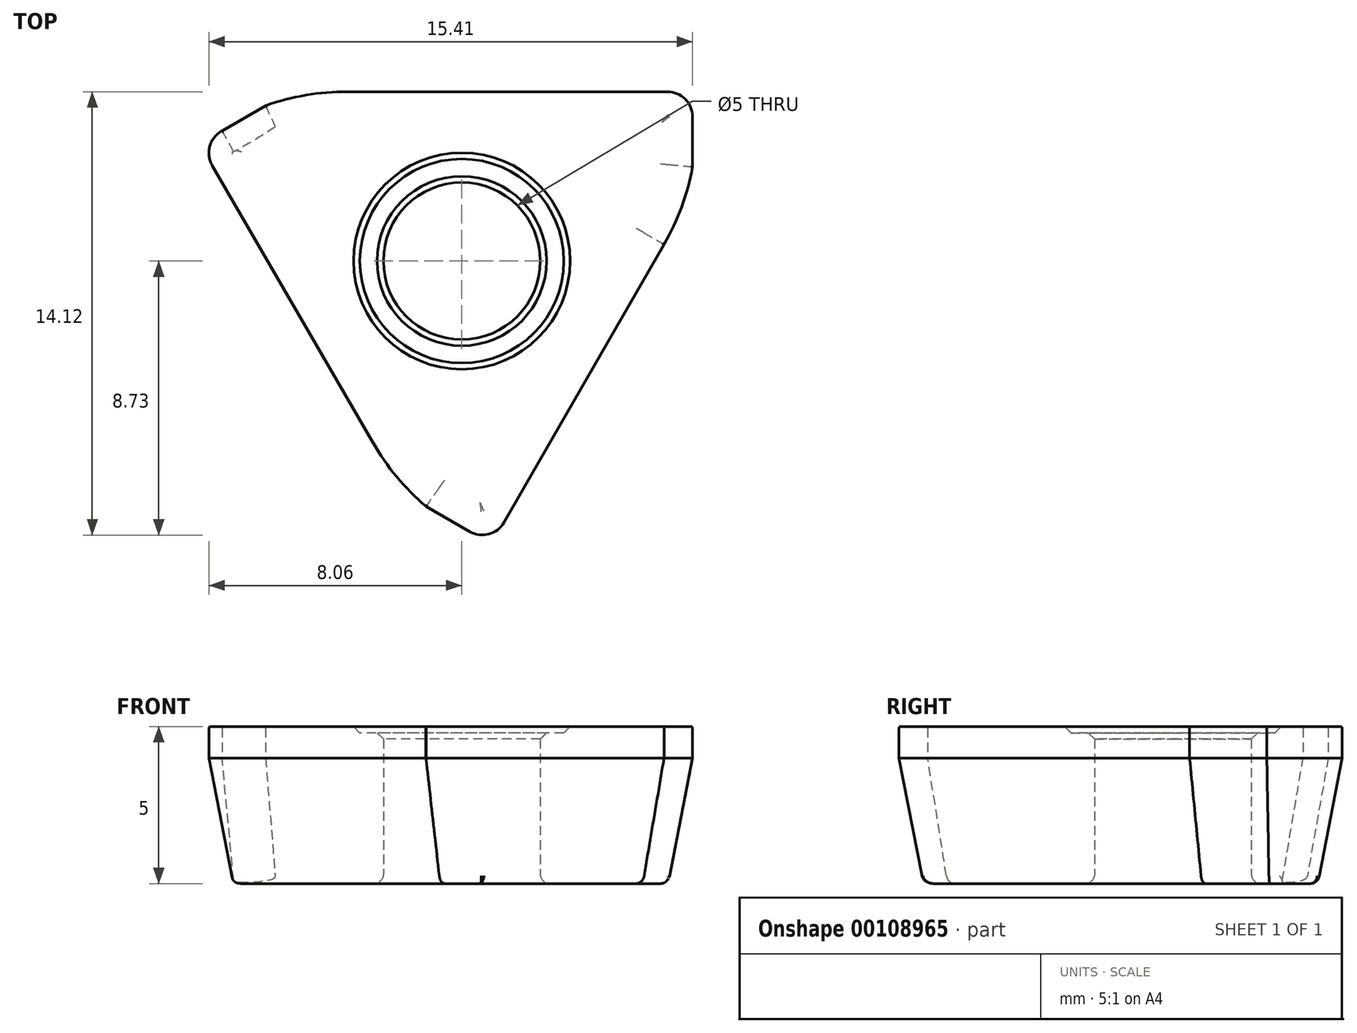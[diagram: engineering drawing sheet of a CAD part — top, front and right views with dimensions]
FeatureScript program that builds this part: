
annotation { "Feature Type Name" : "Feature", "Feature Type Description" : "" }
export const myFeature = defineFeature(function(context is Context, id is Id, definition is map)
    precondition{}
    {
        {
            var Q0;
            Q0=qCreatedBy(makeId("Top.planeOp"),FACE);
            var sketch = newSketch(context, id + "F0", { "sketchPlane" : qUnion([Q0])});
            skLineSegment(sketch, "E0", {"start": v(-2.83, -5.78) * mm, "end": v(-7.95, 3.04) * mm});
            skLineSegment(sketch, "E1", {"start": v(7.35, 4.6) * mm, "end": v(7.35, 3) * mm});
            skLineSegment(sketch, "E2", {"start": v(0.25, -8.62) * mm, "end": v(-1.13, -7.82) * mm});
            skPoint(sketch, "E3.orphan", {"position": v(0, -10.66) * mm});
            skPoint(sketch, "E4.visualSharp", {"position": v(-8.35, 3.74) * mm});
            skArc(sketch, "E4.filletArc", {"start": v(-7.64, 4.15) * mm, "mid": v(-8.03, 3.66) * mm, "end": v(-7.95, 3.04) * mm});
            skPoint(sketch, "E5.visualSharp", {"position": v(0.95, -9.02) * mm});
            skArc(sketch, "E5.filletArc", {"start": v(0.25, -8.62) * mm, "mid": v(0.86, -8.7) * mm, "end": v(1.34, -8.33) * mm});
            skPoint(sketch, "E6.visualSharp", {"position": v(7.35, 5.4) * mm});
            skArc(sketch, "E6.filletArc", {"start": v(7.35, 4.6) * mm, "mid": v(7.12, 5.16) * mm, "end": v(6.55, 5.4) * mm});
            skPoint(sketch, "E7", {"position": v(-6.25, 4.95) * mm});
            skPoint(sketch, "E8", {"position": v(-3.65, 5.4) * mm});
            skPoint(sketch, "E9", {"position": v(7.35, 3) * mm});
            skPoint(sketch, "E10", {"position": v(-1.13, -7.82) * mm});
            skPoint(sketch, "E11", {"position": v(-2.83, -5.78) * mm});
            skPoint(sketch, "E12", {"position": v(6.43, 0.51) * mm});
            skCircle(sketch, "E13", {"center": v(0, 0) * mm, "radius": 2.5 * mm});
            skArc(sketch, "E14", {"start": v(-3.65, 5.4) * mm, "mid": v(-4.97, 5.28) * mm, "end": v(-6.25, 4.95) * mm});
            skLineSegment(sketch, "E15", {"start": v(-7.64, 4.15) * mm, "end": v(-6.25, 4.95) * mm});
            skLineSegment(sketch, "E16", {"start": v(-3.65, 5.4) * mm, "end": v(6.55, 5.4) * mm});
            skArc(sketch, "E17.1.0", {"start": v(-2.83, -5.78) * mm, "mid": v(-2.08, -6.87) * mm, "end": v(-1.15, -7.81) * mm});
            skArc(sketch, "E17.2.0", {"start": v(6.44, 0.53) * mm, "mid": v(7, 1.72) * mm, "end": v(7.35, 3) * mm});
            skPoint(sketch, "E17.center", {"position": v(-0.02, 0.04) * mm});
            skPoint(sketch, "E18.orphan", {"position": v(7.35, 2.1) * mm});
            skCircle(sketch, "E19", {"center": v(0, 0) * mm, "radius": 3.25 * mm});
            skLineSegment(sketch, "E20.trimOffspring", {"start": v(6.43, 0.51) * mm, "end": v(1.34, -8.33) * mm});
            skLineSegment(sketch, "E21", {"start": v(6.43, 0.51) * mm, "end": v(6.44, 0.53) * mm});
            skLineSegment(sketch, "E22", {"start": v(-1.15, -7.81) * mm, "end": v(-1.13, -7.82) * mm});
            skSolve(sketch);
        }
        {
            var Q0;
            Q0=makeQuery(id+"F0.imprint","IMPRINT",FACE,{"disambiguationData":[TD([[makeQuery(id+"F0.imprint","IMPRINT",EDGE,{"derivedFrom":sQuery(id+"F0.wireOp",EDGE,"E0")}),-1.0]])]});
            extrude(context, id + "F1", {"entities" : qUnion([Q0]), "depth" : 5 * mm});
        }
        {
            var Q0;
            Q0=makeQuery(id+"F0.imprint","IMPRINT",FACE,{"disambiguationData":[TD([[makeQuery(id+"F0.imprint","IMPRINT",EDGE,{"derivedFrom":sQuery(id+"F0.wireOp",EDGE,"E13")}),-1.0]])]});
            var Q1;
            Q1=makeQuery(id+"F0.imprint","IMPRINT",FACE,{"disambiguationData":[TD([[makeQuery(id+"F0.imprint","IMPRINT",EDGE,{"derivedFrom":sQuery(id+"F0.wireOp",EDGE,"E0")}),-1.0]])]});
            extrude(context, id + "F2", {"entities" : qUnion([Q0, Q1]), "operationType" : NewBodyOperationType.ADD, "depth" : 4.8 * mm});
        }
        {
            var Q0;
            Q0=makeQuery(id+"F1.opExtrude","CAP_EDGE",EDGE,{"disambiguationData":[OSD([sQuery(id+"F0.wireOp",EDGE,"E0")])],"isStart":true});
            var Q1;
            Q1=makeQuery(id+"F1.opExtrude","CAP_EDGE",EDGE,{"disambiguationData":[OSD([sQuery(id+"F0.wireOp",EDGE,"E17.1.0")])],"isStart":true});
            var Q2;
            Q2=makeQuery(id+"F1.opExtrude","CAP_EDGE",EDGE,{"disambiguationData":[OSD([sQuery(id+"F0.wireOp",EDGE,"E16")])],"isStart":true});
            var Q3;
            Q3=makeQuery(id+"F1.opExtrude","CAP_EDGE",EDGE,{"disambiguationData":[OSD([sQuery(id+"F0.wireOp",EDGE,"E15")])],"isStart":true});
            var Q4;
            Q4=makeQuery(id+"F1.opExtrude","CAP_EDGE",EDGE,{"disambiguationData":[OSD([sQuery(id+"F0.wireOp",EDGE,"E4.filletArc")])],"isStart":true});
            var Q5;
            Q5=makeQuery(id+"F1.opExtrude","CAP_EDGE",EDGE,{"disambiguationData":[OSD([sQuery(id+"F0.wireOp",EDGE,"E14")])],"isStart":true});
            var Q6;
            Q6=makeQuery(id+"F1.opExtrude","CAP_EDGE",EDGE,{"disambiguationData":[OSD([sQuery(id+"F0.wireOp",EDGE,"E1")])],"isStart":true});
            var Q7;
            Q7=makeQuery(id+"F1.opExtrude","CAP_EDGE",EDGE,{"disambiguationData":[OSD([sQuery(id+"F0.wireOp",EDGE,"E20.trimOffspring")])],"isStart":true});
            var Q8;
            Q8=makeQuery(id+"F1.opExtrude","CAP_EDGE",EDGE,{"disambiguationData":[OSD([sQuery(id+"F0.wireOp",EDGE,"E6.filletArc")])],"isStart":true});
            var Q9;
            Q9=makeQuery(id+"F1.opExtrude","CAP_EDGE",EDGE,{"disambiguationData":[OSD([sQuery(id+"F0.wireOp",EDGE,"E2")])],"isStart":true});
            var Q10;
            Q10=makeQuery(id+"F1.opExtrude","CAP_EDGE",EDGE,{"disambiguationData":[OSD([sQuery(id+"F0.wireOp",EDGE,"E21")])],"isStart":true});
            var Q11;
            Q11=makeQuery(id+"F1.opExtrude","CAP_EDGE",EDGE,{"disambiguationData":[OSD([sQuery(id+"F0.wireOp",EDGE,"E17.2.0")])],"isStart":true});
            var Q12;
            Q12=makeQuery(id+"F1.opExtrude","CAP_EDGE",EDGE,{"disambiguationData":[OSD([sQuery(id+"F0.wireOp",EDGE,"E5.filletArc")])],"isStart":true});
            chamfer(context, id + "F3", {"entities" : qUnion([Q0, Q1, Q2, Q3, Q4, Q5, Q6, Q7, Q8, Q9, Q10, Q11, Q12]), "chamferType" : ChamferType.OFFSET_ANGLE, "width" : 4 * mm, "oppositeDirection" : true, "angle" : 11 * degree});
        }
        {
            var Q0;
            Q0=makeQuery(id+"F1.opExtrude","CAP_EDGE",EDGE,{"disambiguationData":[OSD([sQuery(id+"F0.wireOp",EDGE,"E0")])],"isStart":false});
            var Q1;
            Q1=makeQuery(id+"F1.opExtrude","CAP_EDGE",EDGE,{"disambiguationData":[OSD([sQuery(id+"F0.wireOp",EDGE,"E4.filletArc")])],"isStart":false});
            var Q2;
            Q2=makeQuery(id+"F1.opExtrude","CAP_EDGE",EDGE,{"disambiguationData":[OSD([sQuery(id+"F0.wireOp",EDGE,"E15")])],"isStart":false});
            var Q3;
            Q3=makeQuery(id+"F1.opExtrude","CAP_EDGE",EDGE,{"disambiguationData":[OSD([sQuery(id+"F0.wireOp",EDGE,"E17.1.0")])],"isStart":false});
            var Q4;
            Q4=makeQuery(id+"F1.opExtrude","CAP_EDGE",EDGE,{"disambiguationData":[OSD([sQuery(id+"F0.wireOp",EDGE,"E2")])],"isStart":false});
            var Q5;
            Q5=makeQuery(id+"F1.opExtrude","CAP_EDGE",EDGE,{"disambiguationData":[OSD([sQuery(id+"F0.wireOp",EDGE,"E16")])],"isStart":false});
            var Q6;
            Q6=makeQuery(id+"F1.opExtrude","CAP_EDGE",EDGE,{"disambiguationData":[OSD([sQuery(id+"F0.wireOp",EDGE,"E14")])],"isStart":false});
            var Q7;
            Q7=makeQuery(id+"F1.opExtrude","CAP_EDGE",EDGE,{"disambiguationData":[OSD([sQuery(id+"F0.wireOp",EDGE,"E17.2.0")])],"isStart":false});
            fillet(context, id + "F4", {"entities" : qUnion([Q0, Q1, Q2, Q3, Q4, Q5, Q6, Q7]), "radius" : 0.05 * mm, "tangentPropagation" : true, "allowEdgeOverflow" : false});
        }
        {
            var Q0;
            {var subQ0=sQuery(id+"F0.wireOp",EDGE,"E22");var subQ1=sQuery(id+"F0.wireOp",EDGE,"E21");var subQ2=sQuery(id+"F0.wireOp",EDGE,"E20.trimOffspring");var subQ3=sQuery(id+"F0.wireOp",EDGE,"E17.2.0");var subQ4=sQuery(id+"F0.wireOp",EDGE,"E17.1.0");var subQ5=sQuery(id+"F0.wireOp",EDGE,"E16");var subQ6=sQuery(id+"F0.wireOp",EDGE,"E15");var subQ7=sQuery(id+"F0.wireOp",EDGE,"E14");var subQ8=sQuery(id+"F0.wireOp",EDGE,"E6.filletArc");var subQ9=sQuery(id+"F0.wireOp",EDGE,"E5.filletArc");var subQ10=sQuery(id+"F0.wireOp",EDGE,"E4.filletArc");var subQ11=sQuery(id+"F0.wireOp",EDGE,"E2");var subQ12=sQuery(id+"F0.wireOp",EDGE,"E1");var subQ13=sQuery(id+"F0.wireOp",EDGE,"E0");Q0=makeQuery(id+"F3.opChamfer","BLEND_EDGE",EDGE,{"blendedFrom":[makeQuery(id+"F1.opExtrude","CAP_EDGE",EDGE,{"disambiguationData":[OSD([subQ5])],"isStart":true}),makeQuery(id+"F2.boolean.opBoolean","MERGE",FACE,{"derivedFrom":[makeQuery(id+"F1.opExtrude","CAP_FACE",FACE,{"disambiguationData":[OSD([subQ13,subQ12,subQ11,subQ10,subQ9,subQ8,subQ7,subQ6,subQ5,subQ4,subQ3,sQuery(id+"F0.wireOp",EDGE,"E19"),subQ2,subQ1,subQ0])],"isStart":true}),makeQuery(id+"F2.opExtrude","CAP_FACE",FACE,{"disambiguationData":[OSD([subQ13,subQ12,subQ11,subQ10,subQ9,subQ8,sQuery(id+"F0.wireOp",EDGE,"E13"),subQ7,subQ6,subQ5,subQ4,subQ3,subQ2,subQ1,subQ0])],"isStart":true})]})],"blendedInto":[makeQuery(id+"F2.boolean.opBoolean","MERGE",FACE,{"derivedFrom":[makeQuery(id+"F1.opExtrude","CAP_FACE",FACE,{"disambiguationData":[OSD([subQ13,subQ12,subQ11,subQ10,subQ9,subQ8,subQ7,subQ6,subQ5,subQ4,subQ3,sQuery(id+"F0.wireOp",EDGE,"E19"),subQ2,subQ1,subQ0])],"isStart":true}),makeQuery(id+"F2.opExtrude","CAP_FACE",FACE,{"disambiguationData":[OSD([subQ13,subQ12,subQ11,subQ10,subQ9,subQ8,sQuery(id+"F0.wireOp",EDGE,"E13"),subQ7,subQ6,subQ5,subQ4,subQ3,subQ2,subQ1,subQ0])],"isStart":true})]})]});}
            var Q1;
            {var subQ0=sQuery(id+"F0.wireOp",EDGE,"E22");var subQ1=sQuery(id+"F0.wireOp",EDGE,"E21");var subQ2=sQuery(id+"F0.wireOp",EDGE,"E20.trimOffspring");var subQ3=sQuery(id+"F0.wireOp",EDGE,"E17.2.0");var subQ4=sQuery(id+"F0.wireOp",EDGE,"E17.1.0");var subQ5=sQuery(id+"F0.wireOp",EDGE,"E16");var subQ6=sQuery(id+"F0.wireOp",EDGE,"E15");var subQ7=sQuery(id+"F0.wireOp",EDGE,"E14");var subQ8=sQuery(id+"F0.wireOp",EDGE,"E6.filletArc");var subQ9=sQuery(id+"F0.wireOp",EDGE,"E5.filletArc");var subQ10=sQuery(id+"F0.wireOp",EDGE,"E4.filletArc");var subQ11=sQuery(id+"F0.wireOp",EDGE,"E2");var subQ12=sQuery(id+"F0.wireOp",EDGE,"E1");var subQ13=sQuery(id+"F0.wireOp",EDGE,"E0");Q1=makeQuery(id+"F3.opChamfer","BLEND_EDGE",EDGE,{"blendedFrom":[makeQuery(id+"F1.opExtrude","CAP_EDGE",EDGE,{"disambiguationData":[OSD([subQ3])],"isStart":true}),makeQuery(id+"F2.boolean.opBoolean","MERGE",FACE,{"derivedFrom":[makeQuery(id+"F1.opExtrude","CAP_FACE",FACE,{"disambiguationData":[OSD([subQ13,subQ12,subQ11,subQ10,subQ9,subQ8,subQ7,subQ6,subQ5,subQ4,subQ3,sQuery(id+"F0.wireOp",EDGE,"E19"),subQ2,subQ1,subQ0])],"isStart":true}),makeQuery(id+"F2.opExtrude","CAP_FACE",FACE,{"disambiguationData":[OSD([subQ13,subQ12,subQ11,subQ10,subQ9,subQ8,sQuery(id+"F0.wireOp",EDGE,"E13"),subQ7,subQ6,subQ5,subQ4,subQ3,subQ2,subQ1,subQ0])],"isStart":true})]})],"blendedInto":[makeQuery(id+"F2.boolean.opBoolean","MERGE",FACE,{"derivedFrom":[makeQuery(id+"F1.opExtrude","CAP_FACE",FACE,{"disambiguationData":[OSD([subQ13,subQ12,subQ11,subQ10,subQ9,subQ8,subQ7,subQ6,subQ5,subQ4,subQ3,sQuery(id+"F0.wireOp",EDGE,"E19"),subQ2,subQ1,subQ0])],"isStart":true}),makeQuery(id+"F2.opExtrude","CAP_FACE",FACE,{"disambiguationData":[OSD([subQ13,subQ12,subQ11,subQ10,subQ9,subQ8,sQuery(id+"F0.wireOp",EDGE,"E13"),subQ7,subQ6,subQ5,subQ4,subQ3,subQ2,subQ1,subQ0])],"isStart":true})]})]});}
            var Q2;
            {var subQ0=sQuery(id+"F0.wireOp",EDGE,"E22");var subQ1=sQuery(id+"F0.wireOp",EDGE,"E21");var subQ2=sQuery(id+"F0.wireOp",EDGE,"E20.trimOffspring");var subQ3=sQuery(id+"F0.wireOp",EDGE,"E17.2.0");var subQ4=sQuery(id+"F0.wireOp",EDGE,"E17.1.0");var subQ5=sQuery(id+"F0.wireOp",EDGE,"E16");var subQ6=sQuery(id+"F0.wireOp",EDGE,"E15");var subQ7=sQuery(id+"F0.wireOp",EDGE,"E14");var subQ8=sQuery(id+"F0.wireOp",EDGE,"E6.filletArc");var subQ9=sQuery(id+"F0.wireOp",EDGE,"E5.filletArc");var subQ10=sQuery(id+"F0.wireOp",EDGE,"E4.filletArc");var subQ11=sQuery(id+"F0.wireOp",EDGE,"E2");var subQ12=sQuery(id+"F0.wireOp",EDGE,"E1");var subQ13=sQuery(id+"F0.wireOp",EDGE,"E0");Q2=makeQuery(id+"F3.opChamfer","BLEND_EDGE",EDGE,{"blendedFrom":[makeQuery(id+"F1.opExtrude","CAP_EDGE",EDGE,{"disambiguationData":[OSD([subQ11])],"isStart":true}),makeQuery(id+"F2.boolean.opBoolean","MERGE",FACE,{"derivedFrom":[makeQuery(id+"F1.opExtrude","CAP_FACE",FACE,{"disambiguationData":[OSD([subQ13,subQ12,subQ11,subQ10,subQ9,subQ8,subQ7,subQ6,subQ5,subQ4,subQ3,sQuery(id+"F0.wireOp",EDGE,"E19"),subQ2,subQ1,subQ0])],"isStart":true}),makeQuery(id+"F2.opExtrude","CAP_FACE",FACE,{"disambiguationData":[OSD([subQ13,subQ12,subQ11,subQ10,subQ9,subQ8,sQuery(id+"F0.wireOp",EDGE,"E13"),subQ7,subQ6,subQ5,subQ4,subQ3,subQ2,subQ1,subQ0])],"isStart":true})]})],"blendedInto":[makeQuery(id+"F2.boolean.opBoolean","MERGE",FACE,{"derivedFrom":[makeQuery(id+"F1.opExtrude","CAP_FACE",FACE,{"disambiguationData":[OSD([subQ13,subQ12,subQ11,subQ10,subQ9,subQ8,subQ7,subQ6,subQ5,subQ4,subQ3,sQuery(id+"F0.wireOp",EDGE,"E19"),subQ2,subQ1,subQ0])],"isStart":true}),makeQuery(id+"F2.opExtrude","CAP_FACE",FACE,{"disambiguationData":[OSD([subQ13,subQ12,subQ11,subQ10,subQ9,subQ8,sQuery(id+"F0.wireOp",EDGE,"E13"),subQ7,subQ6,subQ5,subQ4,subQ3,subQ2,subQ1,subQ0])],"isStart":true})]})]});}
            var Q3;
            {var subQ0=sQuery(id+"F0.wireOp",EDGE,"E22");var subQ1=sQuery(id+"F0.wireOp",EDGE,"E21");var subQ2=sQuery(id+"F0.wireOp",EDGE,"E20.trimOffspring");var subQ3=sQuery(id+"F0.wireOp",EDGE,"E17.2.0");var subQ4=sQuery(id+"F0.wireOp",EDGE,"E17.1.0");var subQ5=sQuery(id+"F0.wireOp",EDGE,"E16");var subQ6=sQuery(id+"F0.wireOp",EDGE,"E15");var subQ7=sQuery(id+"F0.wireOp",EDGE,"E14");var subQ8=sQuery(id+"F0.wireOp",EDGE,"E6.filletArc");var subQ9=sQuery(id+"F0.wireOp",EDGE,"E5.filletArc");var subQ10=sQuery(id+"F0.wireOp",EDGE,"E4.filletArc");var subQ11=sQuery(id+"F0.wireOp",EDGE,"E2");var subQ12=sQuery(id+"F0.wireOp",EDGE,"E1");var subQ13=sQuery(id+"F0.wireOp",EDGE,"E0");Q3=makeQuery(id+"F3.opChamfer","BLEND_EDGE",EDGE,{"blendedFrom":[makeQuery(id+"F1.opExtrude","CAP_EDGE",EDGE,{"disambiguationData":[OSD([subQ9])],"isStart":true}),makeQuery(id+"F2.boolean.opBoolean","MERGE",FACE,{"derivedFrom":[makeQuery(id+"F1.opExtrude","CAP_FACE",FACE,{"disambiguationData":[OSD([subQ13,subQ12,subQ11,subQ10,subQ9,subQ8,subQ7,subQ6,subQ5,subQ4,subQ3,sQuery(id+"F0.wireOp",EDGE,"E19"),subQ2,subQ1,subQ0])],"isStart":true}),makeQuery(id+"F2.opExtrude","CAP_FACE",FACE,{"disambiguationData":[OSD([subQ13,subQ12,subQ11,subQ10,subQ9,subQ8,sQuery(id+"F0.wireOp",EDGE,"E13"),subQ7,subQ6,subQ5,subQ4,subQ3,subQ2,subQ1,subQ0])],"isStart":true})]})],"blendedInto":[makeQuery(id+"F2.boolean.opBoolean","MERGE",FACE,{"derivedFrom":[makeQuery(id+"F1.opExtrude","CAP_FACE",FACE,{"disambiguationData":[OSD([subQ13,subQ12,subQ11,subQ10,subQ9,subQ8,subQ7,subQ6,subQ5,subQ4,subQ3,sQuery(id+"F0.wireOp",EDGE,"E19"),subQ2,subQ1,subQ0])],"isStart":true}),makeQuery(id+"F2.opExtrude","CAP_FACE",FACE,{"disambiguationData":[OSD([subQ13,subQ12,subQ11,subQ10,subQ9,subQ8,sQuery(id+"F0.wireOp",EDGE,"E13"),subQ7,subQ6,subQ5,subQ4,subQ3,subQ2,subQ1,subQ0])],"isStart":true})]})]});}
            var Q4;
            {var subQ0=sQuery(id+"F0.wireOp",EDGE,"E22");var subQ1=sQuery(id+"F0.wireOp",EDGE,"E21");var subQ2=sQuery(id+"F0.wireOp",EDGE,"E20.trimOffspring");var subQ3=sQuery(id+"F0.wireOp",EDGE,"E17.2.0");var subQ4=sQuery(id+"F0.wireOp",EDGE,"E17.1.0");var subQ5=sQuery(id+"F0.wireOp",EDGE,"E16");var subQ6=sQuery(id+"F0.wireOp",EDGE,"E15");var subQ7=sQuery(id+"F0.wireOp",EDGE,"E14");var subQ8=sQuery(id+"F0.wireOp",EDGE,"E6.filletArc");var subQ9=sQuery(id+"F0.wireOp",EDGE,"E5.filletArc");var subQ10=sQuery(id+"F0.wireOp",EDGE,"E4.filletArc");var subQ11=sQuery(id+"F0.wireOp",EDGE,"E2");var subQ12=sQuery(id+"F0.wireOp",EDGE,"E1");var subQ13=sQuery(id+"F0.wireOp",EDGE,"E0");Q4=makeQuery(id+"F3.opChamfer","BLEND_EDGE",EDGE,{"blendedFrom":[makeQuery(id+"F1.opExtrude","CAP_EDGE",EDGE,{"disambiguationData":[OSD([subQ2])],"isStart":true}),makeQuery(id+"F2.boolean.opBoolean","MERGE",FACE,{"derivedFrom":[makeQuery(id+"F1.opExtrude","CAP_FACE",FACE,{"disambiguationData":[OSD([subQ13,subQ12,subQ11,subQ10,subQ9,subQ8,subQ7,subQ6,subQ5,subQ4,subQ3,sQuery(id+"F0.wireOp",EDGE,"E19"),subQ2,subQ1,subQ0])],"isStart":true}),makeQuery(id+"F2.opExtrude","CAP_FACE",FACE,{"disambiguationData":[OSD([subQ13,subQ12,subQ11,subQ10,subQ9,subQ8,sQuery(id+"F0.wireOp",EDGE,"E13"),subQ7,subQ6,subQ5,subQ4,subQ3,subQ2,subQ1,subQ0])],"isStart":true})]})],"blendedInto":[makeQuery(id+"F2.boolean.opBoolean","MERGE",FACE,{"derivedFrom":[makeQuery(id+"F1.opExtrude","CAP_FACE",FACE,{"disambiguationData":[OSD([subQ13,subQ12,subQ11,subQ10,subQ9,subQ8,subQ7,subQ6,subQ5,subQ4,subQ3,sQuery(id+"F0.wireOp",EDGE,"E19"),subQ2,subQ1,subQ0])],"isStart":true}),makeQuery(id+"F2.opExtrude","CAP_FACE",FACE,{"disambiguationData":[OSD([subQ13,subQ12,subQ11,subQ10,subQ9,subQ8,sQuery(id+"F0.wireOp",EDGE,"E13"),subQ7,subQ6,subQ5,subQ4,subQ3,subQ2,subQ1,subQ0])],"isStart":true})]})]});}
            var Q5;
            {var subQ0=sQuery(id+"F0.wireOp",EDGE,"E22");var subQ1=sQuery(id+"F0.wireOp",EDGE,"E21");var subQ2=sQuery(id+"F0.wireOp",EDGE,"E20.trimOffspring");var subQ3=sQuery(id+"F0.wireOp",EDGE,"E17.2.0");var subQ4=sQuery(id+"F0.wireOp",EDGE,"E17.1.0");var subQ5=sQuery(id+"F0.wireOp",EDGE,"E16");var subQ6=sQuery(id+"F0.wireOp",EDGE,"E15");var subQ7=sQuery(id+"F0.wireOp",EDGE,"E14");var subQ8=sQuery(id+"F0.wireOp",EDGE,"E6.filletArc");var subQ9=sQuery(id+"F0.wireOp",EDGE,"E5.filletArc");var subQ10=sQuery(id+"F0.wireOp",EDGE,"E4.filletArc");var subQ11=sQuery(id+"F0.wireOp",EDGE,"E2");var subQ12=sQuery(id+"F0.wireOp",EDGE,"E1");var subQ13=sQuery(id+"F0.wireOp",EDGE,"E0");Q5=makeQuery(id+"F3.opChamfer","BLEND_EDGE",EDGE,{"blendedFrom":[makeQuery(id+"F1.opExtrude","CAP_EDGE",EDGE,{"disambiguationData":[OSD([subQ4])],"isStart":true}),makeQuery(id+"F2.boolean.opBoolean","MERGE",FACE,{"derivedFrom":[makeQuery(id+"F1.opExtrude","CAP_FACE",FACE,{"disambiguationData":[OSD([subQ13,subQ12,subQ11,subQ10,subQ9,subQ8,subQ7,subQ6,subQ5,subQ4,subQ3,sQuery(id+"F0.wireOp",EDGE,"E19"),subQ2,subQ1,subQ0])],"isStart":true}),makeQuery(id+"F2.opExtrude","CAP_FACE",FACE,{"disambiguationData":[OSD([subQ13,subQ12,subQ11,subQ10,subQ9,subQ8,sQuery(id+"F0.wireOp",EDGE,"E13"),subQ7,subQ6,subQ5,subQ4,subQ3,subQ2,subQ1,subQ0])],"isStart":true})]})],"blendedInto":[makeQuery(id+"F2.boolean.opBoolean","MERGE",FACE,{"derivedFrom":[makeQuery(id+"F1.opExtrude","CAP_FACE",FACE,{"disambiguationData":[OSD([subQ13,subQ12,subQ11,subQ10,subQ9,subQ8,subQ7,subQ6,subQ5,subQ4,subQ3,sQuery(id+"F0.wireOp",EDGE,"E19"),subQ2,subQ1,subQ0])],"isStart":true}),makeQuery(id+"F2.opExtrude","CAP_FACE",FACE,{"disambiguationData":[OSD([subQ13,subQ12,subQ11,subQ10,subQ9,subQ8,sQuery(id+"F0.wireOp",EDGE,"E13"),subQ7,subQ6,subQ5,subQ4,subQ3,subQ2,subQ1,subQ0])],"isStart":true})]})]});}
            var Q6;
            {var subQ0=sQuery(id+"F0.wireOp",EDGE,"E22");var subQ1=sQuery(id+"F0.wireOp",EDGE,"E21");var subQ2=sQuery(id+"F0.wireOp",EDGE,"E20.trimOffspring");var subQ3=sQuery(id+"F0.wireOp",EDGE,"E17.2.0");var subQ4=sQuery(id+"F0.wireOp",EDGE,"E17.1.0");var subQ5=sQuery(id+"F0.wireOp",EDGE,"E16");var subQ6=sQuery(id+"F0.wireOp",EDGE,"E15");var subQ7=sQuery(id+"F0.wireOp",EDGE,"E14");var subQ8=sQuery(id+"F0.wireOp",EDGE,"E6.filletArc");var subQ9=sQuery(id+"F0.wireOp",EDGE,"E5.filletArc");var subQ10=sQuery(id+"F0.wireOp",EDGE,"E4.filletArc");var subQ11=sQuery(id+"F0.wireOp",EDGE,"E2");var subQ12=sQuery(id+"F0.wireOp",EDGE,"E1");var subQ13=sQuery(id+"F0.wireOp",EDGE,"E0");Q6=makeQuery(id+"F3.opChamfer","BLEND_EDGE",EDGE,{"blendedFrom":[makeQuery(id+"F1.opExtrude","CAP_EDGE",EDGE,{"disambiguationData":[OSD([subQ7])],"isStart":true}),makeQuery(id+"F2.boolean.opBoolean","MERGE",FACE,{"derivedFrom":[makeQuery(id+"F1.opExtrude","CAP_FACE",FACE,{"disambiguationData":[OSD([subQ13,subQ12,subQ11,subQ10,subQ9,subQ8,subQ7,subQ6,subQ5,subQ4,subQ3,sQuery(id+"F0.wireOp",EDGE,"E19"),subQ2,subQ1,subQ0])],"isStart":true}),makeQuery(id+"F2.opExtrude","CAP_FACE",FACE,{"disambiguationData":[OSD([subQ13,subQ12,subQ11,subQ10,subQ9,subQ8,sQuery(id+"F0.wireOp",EDGE,"E13"),subQ7,subQ6,subQ5,subQ4,subQ3,subQ2,subQ1,subQ0])],"isStart":true})]})],"blendedInto":[makeQuery(id+"F2.boolean.opBoolean","MERGE",FACE,{"derivedFrom":[makeQuery(id+"F1.opExtrude","CAP_FACE",FACE,{"disambiguationData":[OSD([subQ13,subQ12,subQ11,subQ10,subQ9,subQ8,subQ7,subQ6,subQ5,subQ4,subQ3,sQuery(id+"F0.wireOp",EDGE,"E19"),subQ2,subQ1,subQ0])],"isStart":true}),makeQuery(id+"F2.opExtrude","CAP_FACE",FACE,{"disambiguationData":[OSD([subQ13,subQ12,subQ11,subQ10,subQ9,subQ8,sQuery(id+"F0.wireOp",EDGE,"E13"),subQ7,subQ6,subQ5,subQ4,subQ3,subQ2,subQ1,subQ0])],"isStart":true})]})]});}
            var Q7;
            {var subQ0=sQuery(id+"F0.wireOp",EDGE,"E22");var subQ1=sQuery(id+"F0.wireOp",EDGE,"E21");var subQ2=sQuery(id+"F0.wireOp",EDGE,"E20.trimOffspring");var subQ3=sQuery(id+"F0.wireOp",EDGE,"E17.2.0");var subQ4=sQuery(id+"F0.wireOp",EDGE,"E17.1.0");var subQ5=sQuery(id+"F0.wireOp",EDGE,"E16");var subQ6=sQuery(id+"F0.wireOp",EDGE,"E15");var subQ7=sQuery(id+"F0.wireOp",EDGE,"E14");var subQ8=sQuery(id+"F0.wireOp",EDGE,"E6.filletArc");var subQ9=sQuery(id+"F0.wireOp",EDGE,"E5.filletArc");var subQ10=sQuery(id+"F0.wireOp",EDGE,"E4.filletArc");var subQ11=sQuery(id+"F0.wireOp",EDGE,"E2");var subQ12=sQuery(id+"F0.wireOp",EDGE,"E1");var subQ13=sQuery(id+"F0.wireOp",EDGE,"E0");Q7=makeQuery(id+"F3.opChamfer","BLEND_EDGE",EDGE,{"blendedFrom":[makeQuery(id+"F1.opExtrude","CAP_EDGE",EDGE,{"disambiguationData":[OSD([subQ8])],"isStart":true}),makeQuery(id+"F2.boolean.opBoolean","MERGE",FACE,{"derivedFrom":[makeQuery(id+"F1.opExtrude","CAP_FACE",FACE,{"disambiguationData":[OSD([subQ13,subQ12,subQ11,subQ10,subQ9,subQ8,subQ7,subQ6,subQ5,subQ4,subQ3,sQuery(id+"F0.wireOp",EDGE,"E19"),subQ2,subQ1,subQ0])],"isStart":true}),makeQuery(id+"F2.opExtrude","CAP_FACE",FACE,{"disambiguationData":[OSD([subQ13,subQ12,subQ11,subQ10,subQ9,subQ8,sQuery(id+"F0.wireOp",EDGE,"E13"),subQ7,subQ6,subQ5,subQ4,subQ3,subQ2,subQ1,subQ0])],"isStart":true})]})],"blendedInto":[makeQuery(id+"F2.boolean.opBoolean","MERGE",FACE,{"derivedFrom":[makeQuery(id+"F1.opExtrude","CAP_FACE",FACE,{"disambiguationData":[OSD([subQ13,subQ12,subQ11,subQ10,subQ9,subQ8,subQ7,subQ6,subQ5,subQ4,subQ3,sQuery(id+"F0.wireOp",EDGE,"E19"),subQ2,subQ1,subQ0])],"isStart":true}),makeQuery(id+"F2.opExtrude","CAP_FACE",FACE,{"disambiguationData":[OSD([subQ13,subQ12,subQ11,subQ10,subQ9,subQ8,sQuery(id+"F0.wireOp",EDGE,"E13"),subQ7,subQ6,subQ5,subQ4,subQ3,subQ2,subQ1,subQ0])],"isStart":true})]})]});}
            var Q8;
            {var subQ0=sQuery(id+"F0.wireOp",EDGE,"E22");var subQ1=sQuery(id+"F0.wireOp",EDGE,"E21");var subQ2=sQuery(id+"F0.wireOp",EDGE,"E20.trimOffspring");var subQ3=sQuery(id+"F0.wireOp",EDGE,"E17.2.0");var subQ4=sQuery(id+"F0.wireOp",EDGE,"E17.1.0");var subQ5=sQuery(id+"F0.wireOp",EDGE,"E16");var subQ6=sQuery(id+"F0.wireOp",EDGE,"E15");var subQ7=sQuery(id+"F0.wireOp",EDGE,"E14");var subQ8=sQuery(id+"F0.wireOp",EDGE,"E6.filletArc");var subQ9=sQuery(id+"F0.wireOp",EDGE,"E5.filletArc");var subQ10=sQuery(id+"F0.wireOp",EDGE,"E4.filletArc");var subQ11=sQuery(id+"F0.wireOp",EDGE,"E2");var subQ12=sQuery(id+"F0.wireOp",EDGE,"E1");var subQ13=sQuery(id+"F0.wireOp",EDGE,"E0");Q8=makeQuery(id+"F3.opChamfer","BLEND_EDGE",EDGE,{"blendedFrom":[makeQuery(id+"F1.opExtrude","CAP_EDGE",EDGE,{"disambiguationData":[OSD([subQ12])],"isStart":true}),makeQuery(id+"F2.boolean.opBoolean","MERGE",FACE,{"derivedFrom":[makeQuery(id+"F1.opExtrude","CAP_FACE",FACE,{"disambiguationData":[OSD([subQ13,subQ12,subQ11,subQ10,subQ9,subQ8,subQ7,subQ6,subQ5,subQ4,subQ3,sQuery(id+"F0.wireOp",EDGE,"E19"),subQ2,subQ1,subQ0])],"isStart":true}),makeQuery(id+"F2.opExtrude","CAP_FACE",FACE,{"disambiguationData":[OSD([subQ13,subQ12,subQ11,subQ10,subQ9,subQ8,sQuery(id+"F0.wireOp",EDGE,"E13"),subQ7,subQ6,subQ5,subQ4,subQ3,subQ2,subQ1,subQ0])],"isStart":true})]})],"blendedInto":[makeQuery(id+"F2.boolean.opBoolean","MERGE",FACE,{"derivedFrom":[makeQuery(id+"F1.opExtrude","CAP_FACE",FACE,{"disambiguationData":[OSD([subQ13,subQ12,subQ11,subQ10,subQ9,subQ8,subQ7,subQ6,subQ5,subQ4,subQ3,sQuery(id+"F0.wireOp",EDGE,"E19"),subQ2,subQ1,subQ0])],"isStart":true}),makeQuery(id+"F2.opExtrude","CAP_FACE",FACE,{"disambiguationData":[OSD([subQ13,subQ12,subQ11,subQ10,subQ9,subQ8,sQuery(id+"F0.wireOp",EDGE,"E13"),subQ7,subQ6,subQ5,subQ4,subQ3,subQ2,subQ1,subQ0])],"isStart":true})]})]});}
            var Q9;
            {var subQ0=sQuery(id+"F0.wireOp",EDGE,"E22");var subQ1=sQuery(id+"F0.wireOp",EDGE,"E21");var subQ2=sQuery(id+"F0.wireOp",EDGE,"E20.trimOffspring");var subQ3=sQuery(id+"F0.wireOp",EDGE,"E17.2.0");var subQ4=sQuery(id+"F0.wireOp",EDGE,"E17.1.0");var subQ5=sQuery(id+"F0.wireOp",EDGE,"E16");var subQ6=sQuery(id+"F0.wireOp",EDGE,"E15");var subQ7=sQuery(id+"F0.wireOp",EDGE,"E14");var subQ8=sQuery(id+"F0.wireOp",EDGE,"E6.filletArc");var subQ9=sQuery(id+"F0.wireOp",EDGE,"E5.filletArc");var subQ10=sQuery(id+"F0.wireOp",EDGE,"E4.filletArc");var subQ11=sQuery(id+"F0.wireOp",EDGE,"E2");var subQ12=sQuery(id+"F0.wireOp",EDGE,"E1");var subQ13=sQuery(id+"F0.wireOp",EDGE,"E0");Q9=makeQuery(id+"F3.opChamfer","BLEND_EDGE",EDGE,{"blendedFrom":[makeQuery(id+"F1.opExtrude","CAP_EDGE",EDGE,{"disambiguationData":[OSD([subQ13])],"isStart":true}),makeQuery(id+"F2.boolean.opBoolean","MERGE",FACE,{"derivedFrom":[makeQuery(id+"F1.opExtrude","CAP_FACE",FACE,{"disambiguationData":[OSD([subQ13,subQ12,subQ11,subQ10,subQ9,subQ8,subQ7,subQ6,subQ5,subQ4,subQ3,sQuery(id+"F0.wireOp",EDGE,"E19"),subQ2,subQ1,subQ0])],"isStart":true}),makeQuery(id+"F2.opExtrude","CAP_FACE",FACE,{"disambiguationData":[OSD([subQ13,subQ12,subQ11,subQ10,subQ9,subQ8,sQuery(id+"F0.wireOp",EDGE,"E13"),subQ7,subQ6,subQ5,subQ4,subQ3,subQ2,subQ1,subQ0])],"isStart":true})]})],"blendedInto":[makeQuery(id+"F2.boolean.opBoolean","MERGE",FACE,{"derivedFrom":[makeQuery(id+"F1.opExtrude","CAP_FACE",FACE,{"disambiguationData":[OSD([subQ13,subQ12,subQ11,subQ10,subQ9,subQ8,subQ7,subQ6,subQ5,subQ4,subQ3,sQuery(id+"F0.wireOp",EDGE,"E19"),subQ2,subQ1,subQ0])],"isStart":true}),makeQuery(id+"F2.opExtrude","CAP_FACE",FACE,{"disambiguationData":[OSD([subQ13,subQ12,subQ11,subQ10,subQ9,subQ8,sQuery(id+"F0.wireOp",EDGE,"E13"),subQ7,subQ6,subQ5,subQ4,subQ3,subQ2,subQ1,subQ0])],"isStart":true})]})]});}
            var Q10;
            {var subQ0=sQuery(id+"F0.wireOp",EDGE,"E22");var subQ1=sQuery(id+"F0.wireOp",EDGE,"E21");var subQ2=sQuery(id+"F0.wireOp",EDGE,"E20.trimOffspring");var subQ3=sQuery(id+"F0.wireOp",EDGE,"E17.2.0");var subQ4=sQuery(id+"F0.wireOp",EDGE,"E17.1.0");var subQ5=sQuery(id+"F0.wireOp",EDGE,"E16");var subQ6=sQuery(id+"F0.wireOp",EDGE,"E15");var subQ7=sQuery(id+"F0.wireOp",EDGE,"E14");var subQ8=sQuery(id+"F0.wireOp",EDGE,"E6.filletArc");var subQ9=sQuery(id+"F0.wireOp",EDGE,"E5.filletArc");var subQ10=sQuery(id+"F0.wireOp",EDGE,"E4.filletArc");var subQ11=sQuery(id+"F0.wireOp",EDGE,"E2");var subQ12=sQuery(id+"F0.wireOp",EDGE,"E1");var subQ13=sQuery(id+"F0.wireOp",EDGE,"E0");Q10=makeQuery(id+"F3.opChamfer","BLEND_EDGE",EDGE,{"blendedFrom":[makeQuery(id+"F1.opExtrude","CAP_EDGE",EDGE,{"disambiguationData":[OSD([subQ10])],"isStart":true}),makeQuery(id+"F2.boolean.opBoolean","MERGE",FACE,{"derivedFrom":[makeQuery(id+"F1.opExtrude","CAP_FACE",FACE,{"disambiguationData":[OSD([subQ13,subQ12,subQ11,subQ10,subQ9,subQ8,subQ7,subQ6,subQ5,subQ4,subQ3,sQuery(id+"F0.wireOp",EDGE,"E19"),subQ2,subQ1,subQ0])],"isStart":true}),makeQuery(id+"F2.opExtrude","CAP_FACE",FACE,{"disambiguationData":[OSD([subQ13,subQ12,subQ11,subQ10,subQ9,subQ8,sQuery(id+"F0.wireOp",EDGE,"E13"),subQ7,subQ6,subQ5,subQ4,subQ3,subQ2,subQ1,subQ0])],"isStart":true})]})],"blendedInto":[makeQuery(id+"F2.boolean.opBoolean","MERGE",FACE,{"derivedFrom":[makeQuery(id+"F1.opExtrude","CAP_FACE",FACE,{"disambiguationData":[OSD([subQ13,subQ12,subQ11,subQ10,subQ9,subQ8,subQ7,subQ6,subQ5,subQ4,subQ3,sQuery(id+"F0.wireOp",EDGE,"E19"),subQ2,subQ1,subQ0])],"isStart":true}),makeQuery(id+"F2.opExtrude","CAP_FACE",FACE,{"disambiguationData":[OSD([subQ13,subQ12,subQ11,subQ10,subQ9,subQ8,sQuery(id+"F0.wireOp",EDGE,"E13"),subQ7,subQ6,subQ5,subQ4,subQ3,subQ2,subQ1,subQ0])],"isStart":true})]})]});}
            var Q11;
            Q11=makeQuery(id+"F2.opExtrude","CAP_EDGE",EDGE,{"disambiguationData":[OSD([sQuery(id+"F0.wireOp",EDGE,"E13")])],"isStart":true});
            fillet(context, id + "F5", {"entities" : qUnion([Q0, Q1, Q2, Q3, Q4, Q5, Q6, Q7, Q8, Q9, Q10, Q11]), "radius" : 0.3 * mm, "tangentPropagation" : true, "allowEdgeOverflow" : false});
        }
        {
            var Q0;
            Q0=makeQuery(id+"F2.opExtrude","CAP_EDGE",EDGE,{"disambiguationData":[OSD([sQuery(id+"F0.wireOp",EDGE,"E13")])],"isStart":false});
            var Q1;
            Q1=makeQuery(id+"F1.opExtrude","CAP_EDGE",EDGE,{"disambiguationData":[OSD([sQuery(id+"F0.wireOp",EDGE,"E19")])],"isStart":false});
            chamfer(context, id + "F6", {"entities" : qUnion([Q0, Q1]), "width" : 0.2 * mm, "tangentPropagation" : true});
        }
    });
